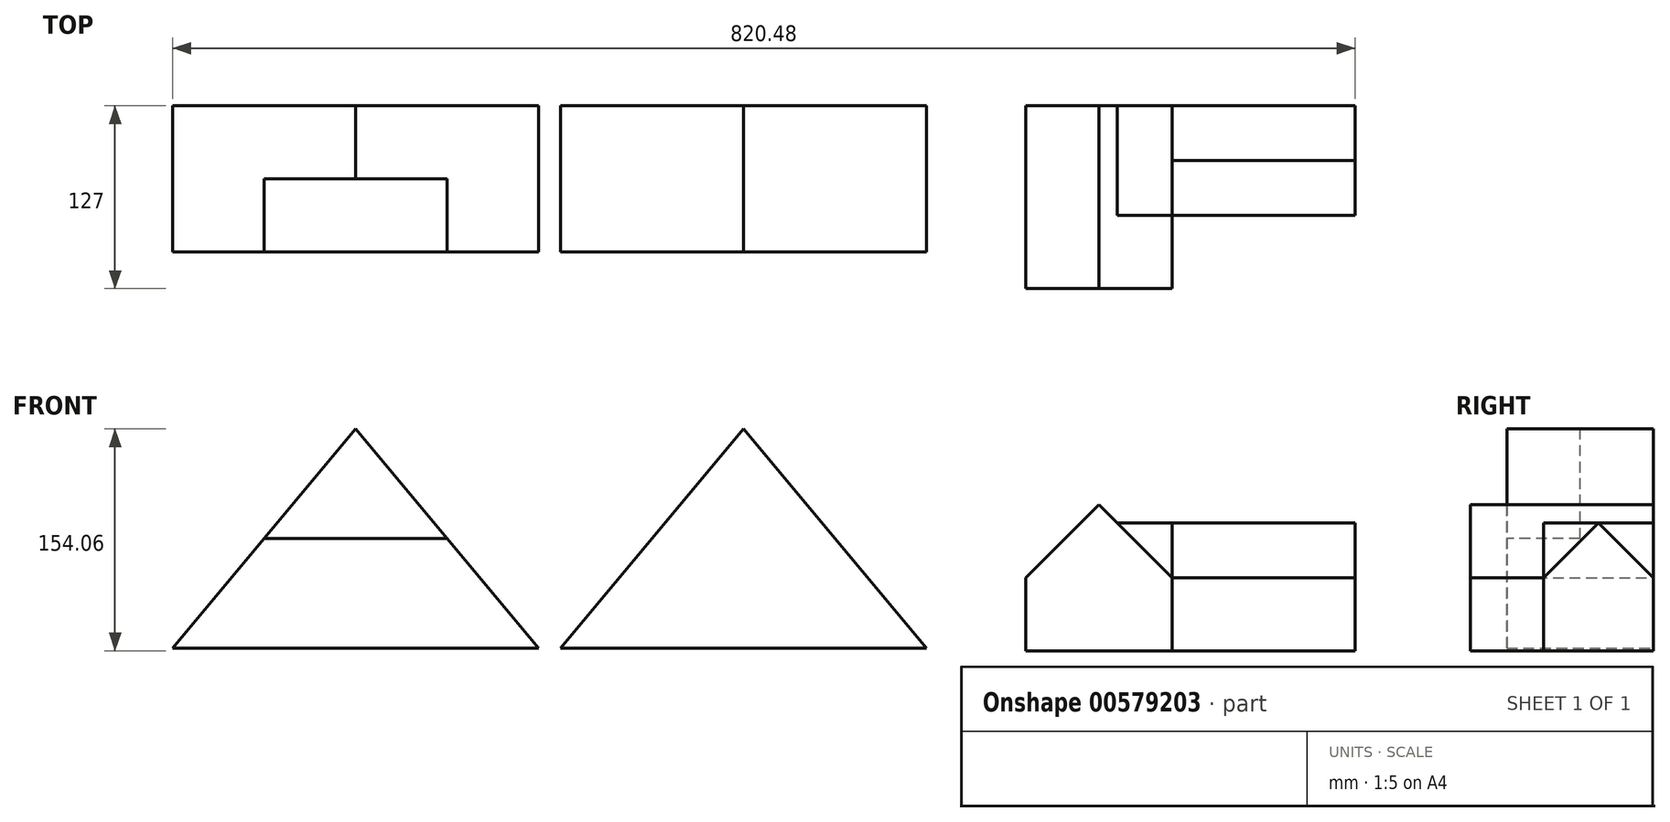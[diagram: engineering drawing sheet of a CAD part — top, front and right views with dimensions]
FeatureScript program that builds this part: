
annotation { "Feature Type Name" : "Feature", "Feature Type Description" : "" }
export const myFeature = defineFeature(function(context is Context, id is Id, definition is map)
    precondition{}
    {
        {
            var Q0;
            Q0=qCreatedBy(makeId("Front.planeOp"),FACE);
            var sketch = newSketch(context, id + "F0", { "sketchPlane" : qUnion([Q0])});
            skLineSegment(sketch, "E0", {"start": v(0, 0) * mm, "end": v(254, 0) * mm});
            skLineSegment(sketch, "E1", {"start": v(0, 0) * mm, "end": v(127, 152.4) * mm});
            skLineSegment(sketch, "E2", {"start": v(127, 152.4) * mm, "end": v(254, 0) * mm});
            skSolve(sketch);
        }
        {
            var Q0;
            Q0=makeQuery(id+"F0.imprint","IMPRINT",FACE,{"disambiguationData":[TD([[makeQuery(id+"F0.imprint","IMPRINT",EDGE,{"derivedFrom":sQuery(id+"F0.wireOp",EDGE,"E0")}),1.0]])]});
            extrude(context, id + "F1", {"entities" : qUnion([Q0]), "depth" : 101.6 * mm, "offsetDistance" : 25.4 * mm});
        }
        {
            var Q0;
            Q0=makeQuery(id+"F1.opExtrude","CAP_FACE",FACE,{"disambiguationData":[OSD([sQuery(id+"F0.wireOp",EDGE,"E0"),sQuery(id+"F0.wireOp",EDGE,"E1"),sQuery(id+"F0.wireOp",EDGE,"E2")])],"isStart":false});
            var sketch = newSketch(context, id + "F2", { "sketchPlane" : qUnion([Q0])});
            skLineSegment(sketch, "E3", {"start": v(127, 76.2) * mm, "end": v(190.5, 76.2) * mm});
            skLineSegment(sketch, "E4", {"start": v(190.5, 76.2) * mm, "end": v(63.5, 76.2) * mm});
            skSolve(sketch);
        }
        {
            var Q0;
            {var subQ0=sQuery(id+"F2.wireOp",EDGE,"E4");var subQ3=makeQuery(id+"F2.imprint","IMPRINT",VERTEX,{"derivedFrom":subQ0});Q0=makeQuery(id+"F2.imprint","IMPRINT",FACE,{"disambiguationData":[TD([[makeQuery(id+"F2.imprint","IMPRINT",EDGE,{"disambiguationData":[TD([[subQ3,1.0]])],"derivedFrom":subQ0}),-1.0]])]});}
            extrude(context, id + "F3", {"entities" : qUnion([Q0]), "operationType" : NewBodyOperationType.REMOVE, "oppositeDirection" : true, "depth" : 50.8 * mm, "offsetDistance" : 25.4 * mm});
        }
        {
            var Q0;
            Q0=qCreatedBy(makeId("Front.planeOp"),FACE);
            var sketch = newSketch(context, id + "F4", { "sketchPlane" : qUnion([Q0])});
            skLineSegment(sketch, "E5", {"start": v(269.26, 0) * mm, "end": v(523.26, 0) * mm});
            skLineSegment(sketch, "E6", {"start": v(269.26, 0) * mm, "end": v(396.26, 152.4) * mm});
            skLineSegment(sketch, "E7", {"start": v(396.26, 152.4) * mm, "end": v(523.26, 0) * mm});
            skSolve(sketch);
        }
        {
            var Q0;
            Q0=makeQuery(id+"F4.imprint","IMPRINT",FACE,{"disambiguationData":[TD([[makeQuery(id+"F4.imprint","IMPRINT",EDGE,{"derivedFrom":sQuery(id+"F4.wireOp",EDGE,"E5")}),1.0]])]});
            extrude(context, id + "F5", {"entities" : qUnion([Q0]), "depth" : 101.6 * mm, "offsetDistance" : 25.4 * mm});
        }
        {
            var Q0;
            Q0=qCreatedBy(makeId("Front.planeOp"),FACE);
            var sketch = newSketch(context, id + "F6", { "sketchPlane" : qUnion([Q0])});
            skLineSegment(sketch, "E8", {"start": v(591.88, -1.66) * mm, "end": v(693.48, -1.66) * mm});
            skLineSegment(sketch, "E9", {"start": v(693.48, -1.66) * mm, "end": v(693.48, 49.14) * mm});
            skLineSegment(sketch, "E10", {"start": v(693.48, 49.14) * mm, "end": v(642.68, 99.94) * mm});
            skLineSegment(sketch, "E11", {"start": v(642.68, 99.94) * mm, "end": v(591.88, 49.14) * mm});
            skLineSegment(sketch, "E12", {"start": v(591.88, 49.14) * mm, "end": v(591.88, -1.66) * mm});
            skLineSegment(sketch, "E13", {"start": v(693.48, -1.66) * mm, "end": v(820.48, -1.66) * mm});
            skLineSegment(sketch, "E14", {"start": v(820.48, -1.66) * mm, "end": v(820.48, 49.14) * mm});
            skLineSegment(sketch, "E15", {"start": v(820.48, 49.14) * mm, "end": v(693.48, 49.14) * mm});
            skLineSegment(sketch, "E16", {"start": v(820.48, 49.14) * mm, "end": v(820.48, 87.24) * mm});
            skLineSegment(sketch, "E17", {"start": v(820.48, 87.24) * mm, "end": v(655.38, 87.24) * mm});
            skSolve(sketch);
        }
        {
            var Q0;
            Q0=makeQuery(id+"F6.imprint","IMPRINT",FACE,{"disambiguationData":[TD([[makeQuery(id+"F6.imprint","IMPRINT",EDGE,{"derivedFrom":sQuery(id+"F6.wireOp",EDGE,"E8")}),1.0]])]});
            extrude(context, id + "F7", {"entities" : qUnion([Q0]), "depth" : 127 * mm, "offsetDistance" : 25.4 * mm});
        }
        {
            var Q0;
            Q0=makeQuery(id+"F6.imprint","IMPRINT",FACE,{"disambiguationData":[TD([[makeQuery(id+"F6.imprint","IMPRINT",EDGE,{"derivedFrom":sQuery(id+"F6.wireOp",EDGE,"E9")}),-1.0]])]});
            extrude(context, id + "F8", {"entities" : qUnion([Q0]), "operationType" : NewBodyOperationType.ADD, "depth" : 76.2 * mm, "offsetDistance" : 25.4 * mm});
        }
        {
            var Q0;
            {var subQ0=sQuery(id+"F6.wireOp",EDGE,"E15");Q0=makeQuery(id+"F6.imprint","IMPRINT",FACE,{"disambiguationData":[TD([[makeQuery(id+"F6.imprint","IMPRINT",EDGE,{"derivedFrom":subQ0}),-1.0]])]});}
            extrude(context, id + "F9", {"entities" : qUnion([Q0]), "operationType" : NewBodyOperationType.ADD, "depth" : 76.2 * mm, "offsetDistance" : 25.4 * mm});
        }
        {
            var Q0;
            Q0=makeQuery(id+"F9.boolean.opBoolean","MERGE",FACE,{"derivedFrom":[makeQuery(id+"F8.opExtrude","SWEPT_FACE",FACE,{"disambiguationData":[OSD([sQuery(id+"F6.wireOp",EDGE,"E14")])]}),makeQuery(id+"F9.opExtrude","SWEPT_FACE",FACE,{"disambiguationData":[OSD([sQuery(id+"F6.wireOp",EDGE,"E16")])]})]});
            var sketch = newSketch(context, id + "F10", { "sketchPlane" : qUnion([Q0])});
            skLineSegment(sketch, "E18", {"start": v(-76.2, 49.14) * mm, "end": v(-76.2, 87.24) * mm});
            skLineSegment(sketch, "E19", {"start": v(-76.2, 87.24) * mm, "end": v(-38.1, 87.24) * mm});
            skLineSegment(sketch, "E20", {"start": v(-38.1, 87.24) * mm, "end": v(-76.2, 49.14) * mm});
            skSolve(sketch);
        }
        {
            var Q0;
            Q0=makeQuery(id+"F10.imprint","IMPRINT",FACE,{"disambiguationData":[TD([[makeQuery(id+"F10.imprint","IMPRINT",EDGE,{"derivedFrom":sQuery(id+"F10.wireOp",EDGE,"E18")}),-1.0]])]});
            extrude(context, id + "F11", {"entities" : qUnion([Q0]), "operationType" : NewBodyOperationType.REMOVE, "oppositeDirection" : true, "depth" : 127 * mm, "offsetDistance" : 25.4 * mm});
        }
        {
            var Q0;
            Q0=makeQuery(id+"F9.boolean.opBoolean","MERGE",FACE,{"derivedFrom":[makeQuery(id+"F8.opExtrude","SWEPT_FACE",FACE,{"disambiguationData":[OSD([sQuery(id+"F6.wireOp",EDGE,"E14")])]}),makeQuery(id+"F9.opExtrude","SWEPT_FACE",FACE,{"disambiguationData":[OSD([sQuery(id+"F6.wireOp",EDGE,"E16")])]})]});
            var sketch = newSketch(context, id + "F12", { "sketchPlane" : qUnion([Q0])});
            skLineSegment(sketch, "E21", {"start": v(-38.1, 87.24) * mm, "end": v(0, 87.24) * mm});
            skLineSegment(sketch, "E22", {"start": v(0, 87.24) * mm, "end": v(0, 49.14) * mm});
            skLineSegment(sketch, "E23", {"start": v(0, 49.14) * mm, "end": v(-38.1, 87.24) * mm});
            skSolve(sketch);
        }
        {
            var Q0;
            Q0=makeQuery(id+"F12.imprint","IMPRINT",FACE,{"disambiguationData":[TD([[makeQuery(id+"F12.imprint","IMPRINT",EDGE,{"derivedFrom":sQuery(id+"F12.wireOp",EDGE,"E21")}),-1.0]])]});
            extrude(context, id + "F13", {"entities" : qUnion([Q0]), "operationType" : NewBodyOperationType.REMOVE, "oppositeDirection" : true, "depth" : 127 * mm, "offsetDistance" : 25.4 * mm});
        }
    });
